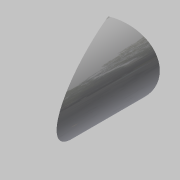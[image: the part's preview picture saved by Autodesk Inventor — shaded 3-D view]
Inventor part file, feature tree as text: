
AUTODESK INVENTOR PART (.ipt)
format: ipt  version: 2017.3 (Build 213257000, 257)  size: 280,576 bytes
history: native  units: in
note: dims shown in document units (in); Inventor stores cm internally (conversion verified against a paired STEP export)
features: extrude x2, other x2, sketch x2
ambient origin geometry x8: Origin, YZ Plane, XZ Plane, XY Plane, X Axis, Y Axis, Z Axis, Center Point
bodies: Solid1 (feature_tree)
feature tree (6):
  extrude  "Extrusion1"  Depth=37.25in
  extrude  "Extrusion2"  Depth=70.0in TaperAngle=0.0deg
  other  "A-Side Definition"
  sketch  "Sketch1"  dims[d0=34.25in d1=37.25in]
  sketch  "Sketch2"  dims[d2=50.9606in d3=17.4961in d4=0.0in d5=0.0in d8=70.0in d9=0.0in d10=34.375in d79=22.5deg]
  other  "Definition1"
